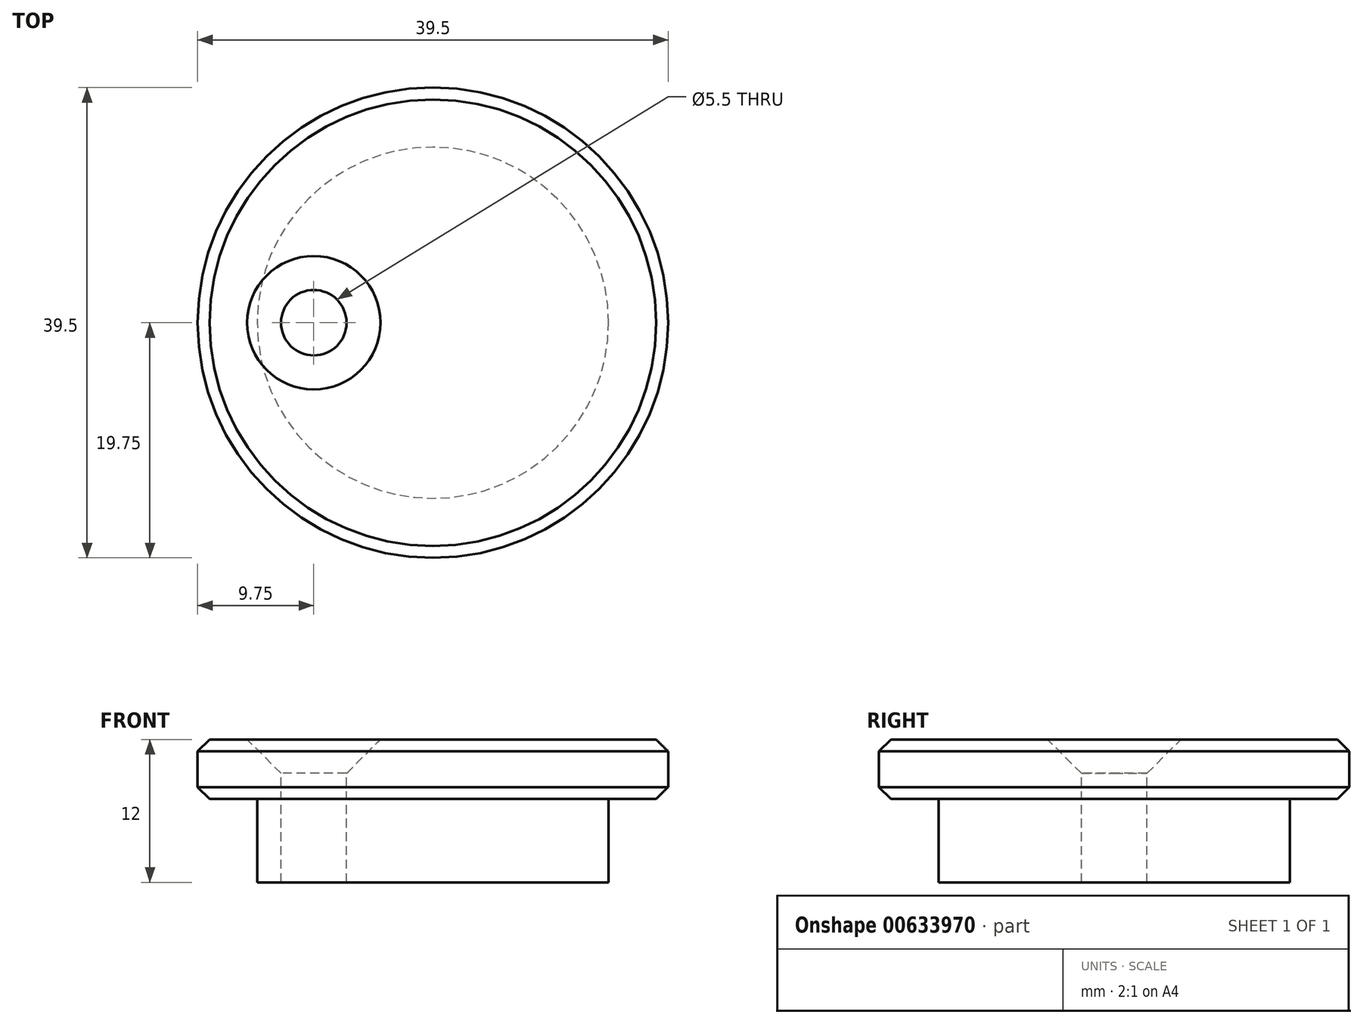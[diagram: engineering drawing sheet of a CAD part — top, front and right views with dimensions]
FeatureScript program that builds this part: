
annotation { "Feature Type Name" : "Feature", "Feature Type Description" : "" }
export const myFeature = defineFeature(function(context is Context, id is Id, definition is map)
    precondition{}
    {
        {
            var Q0;
            Q0=qCreatedBy(makeId("Top.planeOp"),FACE);
            var sketch = newSketch(context, id + "F0", { "sketchPlane" : qUnion([Q0])});
            skCircle(sketch, "E0", {"center": v(0, 0) * mm, "radius": 14.75 * mm});
            skSolve(sketch);
        }
        {
            var Q0;
            Q0=qCreatedBy(makeId("Right.planeOp"),FACE);
            var sketch = newSketch(context, id + "F1", { "sketchPlane" : qUnion([Q0])});
            skLineSegment(sketch, "E1", {"start": v(0, 0) * mm, "end": v(0, 29.93) * mm, "construction": true});
            skSolve(sketch);
        }
        {
            var Q0;
            Q0=makeQuery(id+"F0.imprint","IMPRINT",FACE,{"disambiguationData":[TD([[makeQuery(id+"F0.imprint","IMPRINT",EDGE,{"derivedFrom":sQuery(id+"F0.wireOp",EDGE,"E0")}),1.0]])]});
            extrude(context, id + "F2", {"entities" : qUnion([Q0]), "oppositeDirection" : true, "depth" : 7 * mm, "offsetDistance" : 25 * mm});
        }
        {
            var Q0;
            Q0=makeQuery(id+"F2.opExtrude","CAP_FACE",FACE,{"disambiguationData":[OSD([sQuery(id+"F0.wireOp",EDGE,"E0")])],"isStart":true});
            var sketch = newSketch(context, id + "F3", { "sketchPlane" : qUnion([Q0])});
            skCircle(sketch, "E2.0", {"center": v(0, 0) * mm, "radius": 19.75 * mm});
            skSolve(sketch);
        }
        {
            var Q0;
            Q0=makeQuery(id+"F3.imprint","IMPRINT",FACE,{"disambiguationData":[TD([[makeQuery(id+"F3.imprint","IMPRINT",EDGE,{"derivedFrom":sQuery(id+"F3.wireOp",EDGE,"E2.0")}),1.0]])]});
            var Q1;
            Q1=makeQuery(id+"F3.imprint","IMPRINT",FACE,{"disambiguationData":[TD([[makeQuery(id+"F3.imprint","IMPRINT",EDGE,{"derivedFrom":makeQuery(id+"F2.opExtrude","CAP_EDGE",EDGE,{"disambiguationData":[OSD([sQuery(id+"F0.wireOp",EDGE,"E0")])],"isStart":true})}),1.0]])]});
            extrude(context, id + "F4", {"entities" : qUnion([Q0, Q1]), "operationType" : NewBodyOperationType.ADD, "depth" : 5 * mm, "offsetDistance" : 25 * mm});
        }
        {
            var Q0;
            Q0=makeQuery(id+"F4.opExtrude","CAP_FACE",FACE,{"disambiguationData":[OSD([sQuery(id+"F3.wireOp",EDGE,"E2.0")])],"isStart":false});
            var sketch = newSketch(context, id + "F5", { "sketchPlane" : qUnion([Q0])});
            skLineSegment(sketch, "E3", {"start": v(0, 0) * mm, "end": v(-10, 0) * mm});
            skSolve(sketch);
        }
        {
            var Q0;
            Q0=sQuery(id+"F5.wireOp",VERTEX,"E3.end");
            var Q1;
            Q1=makeQuery(id+"F2.opExtrude","SWEPT_BODY",BODY,{"disambiguationData":[OSD([sQuery(id+"F0.wireOp",EDGE,"E0")])]});
            hole(context, id + "F6", {"style" : HoleStyle.C_SINK, "endStyle" : HoleEndStyle.THROUGH, "standardTappedOrClearance" : lookupTablePath({ "standard" : "ISO", "fit" : "Normal", "size" : "M5", "type" : "Clearance" }), "standardBlindInLast" : lookupTablePath({ "fit" : "Standard", "standard" : "ISO", "size" : "M5", "type" : "Clearance" }), "holeDiameter" : 5.5 * mm, "cSinkDiameter" : 11.2 * mm, "cSinkAngle" : 90 * degree, "majorDiameter" : 5 * mm, "isTappedThrough" : true, "tappedDepth" : 12 * mm, "tapClearance" : 3, "locations" : qUnion([Q0]), "scope" : qUnion([Q1])});
        }
        {
            var Q0;
            Q0=makeQuery(id+"F4.opExtrude","CAP_EDGE",EDGE,{"disambiguationData":[OSD([sQuery(id+"F3.wireOp",EDGE,"E2.0")])],"isStart":false});
            var Q1;
            Q1=makeQuery(id+"F4.opExtrude","CAP_EDGE",EDGE,{"disambiguationData":[OSD([sQuery(id+"F3.wireOp",EDGE,"E2.0")])],"isStart":true});
            chamfer(context, id + "F7", {"entities" : qUnion([Q0, Q1]), "width" : 1 * mm, "tangentPropagation" : true});
        }
    });
